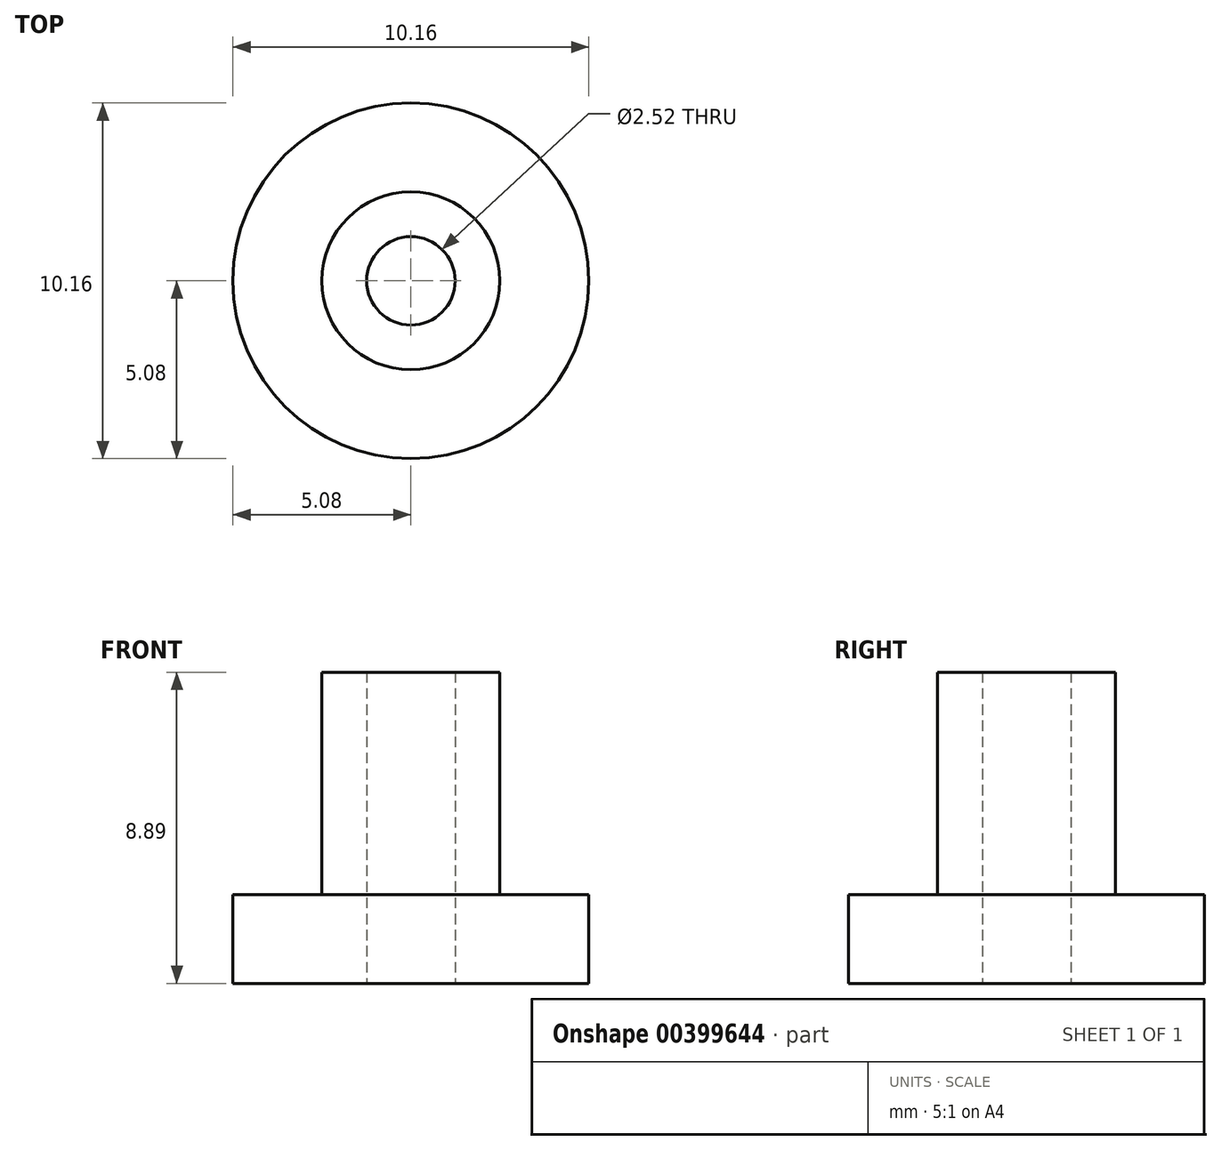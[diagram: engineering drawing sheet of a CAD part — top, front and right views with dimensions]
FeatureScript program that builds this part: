
annotation { "Feature Type Name" : "Feature", "Feature Type Description" : "" }
export const myFeature = defineFeature(function(context is Context, id is Id, definition is map)
    precondition{}
    {
        {
            var Q0;
            Q0=qCreatedBy(makeId("Top.planeOp"),FACE);
            var sketch = newSketch(context, id + "F0", { "sketchPlane" : qUnion([Q0])});
            skCircle(sketch, "E0", {"center": v(0, 0) * mm, "radius": 2.54 * mm});
            skSolve(sketch);
        }
        {
            var Q0;
            Q0 = qSketchRegion(id + "F0", true);
            extrude(context, id + "F1", {"entities" : qUnion([Q0]), "depth" : 8.9 * mm});
        }
        {
            var Q0;
            Q0=makeQuery(id+"F1.opExtrude","CAP_FACE",FACE,{"disambiguationData":[OSD([sQuery(id+"F0.wireOp",EDGE,"E0")])],"isStart":true});
            var sketch = newSketch(context, id + "F2", { "sketchPlane" : qUnion([Q0])});
            skCircle(sketch, "E1", {"center": v(0, 0) * mm, "radius": 5.08 * mm});
            skSolve(sketch);
        }
        {
            var Q0;
            Q0=makeQuery(id+"F2.imprint","IMPRINT",FACE,{"disambiguationData":[TD([[makeQuery(id+"F2.imprint","IMPRINT",EDGE,{"derivedFrom":sQuery(id+"F2.wireOp",EDGE,"E1")}),1.0]])]});
            extrude(context, id + "F3", {"entities" : qUnion([Q0]), "operationType" : NewBodyOperationType.ADD, "oppositeDirection" : true, "depth" : 2.54 * mm});
        }
        {
            var Q0;
            {var subQ0=sQuery(id+"F0.wireOp",EDGE,"E0");Q0=makeQuery(id+"F3.boolean.opBoolean","MERGE",FACE,{"derivedFrom":[makeQuery(id+"F1.opExtrude","CAP_FACE",FACE,{"disambiguationData":[OSD([subQ0])],"isStart":true}),makeQuery(id+"F3.opExtrude","CAP_FACE",FACE,{"disambiguationData":[OSD([subQ0,sQuery(id+"F2.wireOp",EDGE,"E1")])],"isStart":true})]});}
            var sketch = newSketch(context, id + "F4", { "sketchPlane" : qUnion([Q0])});
            skCircle(sketch, "E2", {"center": v(0, 0) * mm, "radius": 1.26 * mm});
            skSolve(sketch);
        }
        {
            var Q0;
            Q0=makeQuery(id+"F4.imprint","IMPRINT",FACE,{"disambiguationData":[TD([[makeQuery(id+"F4.imprint","IMPRINT",EDGE,{"derivedFrom":sQuery(id+"F4.wireOp",EDGE,"E2")}),1.0]])]});
            extrude(context, id + "F5", {"entities" : qUnion([Q0]), "operationType" : NewBodyOperationType.REMOVE, "oppositeDirection" : true, "depth" : 25.4 * mm});
        }
    });
